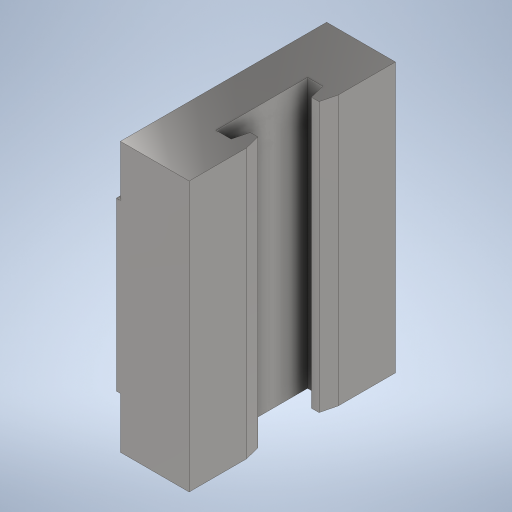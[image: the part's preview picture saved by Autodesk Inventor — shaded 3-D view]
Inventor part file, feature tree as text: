
AUTODESK INVENTOR PART (.ipt)
format: ipt  version: 2023 (Build 270158000, 158)  size: 271,360 bytes
history: native  units: mm
features: sketch x3, extrude x2, hole x1
ambient origin geometry x8: Origin, YZ Plane, XZ Plane, XY Plane, X Axis, Y Axis, Z Axis, Center Point
bodies: Solid1 (feature_tree)
feature tree (6):
  extrude  "Extrusion1"  Depth=9.5mm
  hole  "Hole1"  [1 undecoded]
  extrude  "Extrusion2"  Depth=12.0mm
  sketch  "Sketch1"  dims[d2=8.0mm d3=1.0mm d5=0.5mm d6=4.0mm d8=9.5mm]
  sketch  "Sketch2"  dims[d9=27.0mm d10=35.25mm d11=0.0mm]
  sketch  "Sketch3"  dims[d12=0.0mm d13=12.0mm d14=2.0mm d15=2.0mm d16=20.0mm d17=20.0mm d18=15.0mm d19=15.0mm d20=0.0mm d21=0.0mm d22=35.25mm d23=27.0mm d24=10.125mm d25=3.5mm d26=2.459mm d27=4.0mm d28=3.023mm d29=2.0mm d30=14.3117mm d31=5.0mm d32=20.594885mm d33=35.25mm d34=21.9mm d35=6.675mm d36=0.5mm d37=0.0mm]
note: 1 required parameter value undecoded (feature->parameter linkage not recoverable at this tier; creation-order binding heuristic only, values carry confidence <= 0.55)
